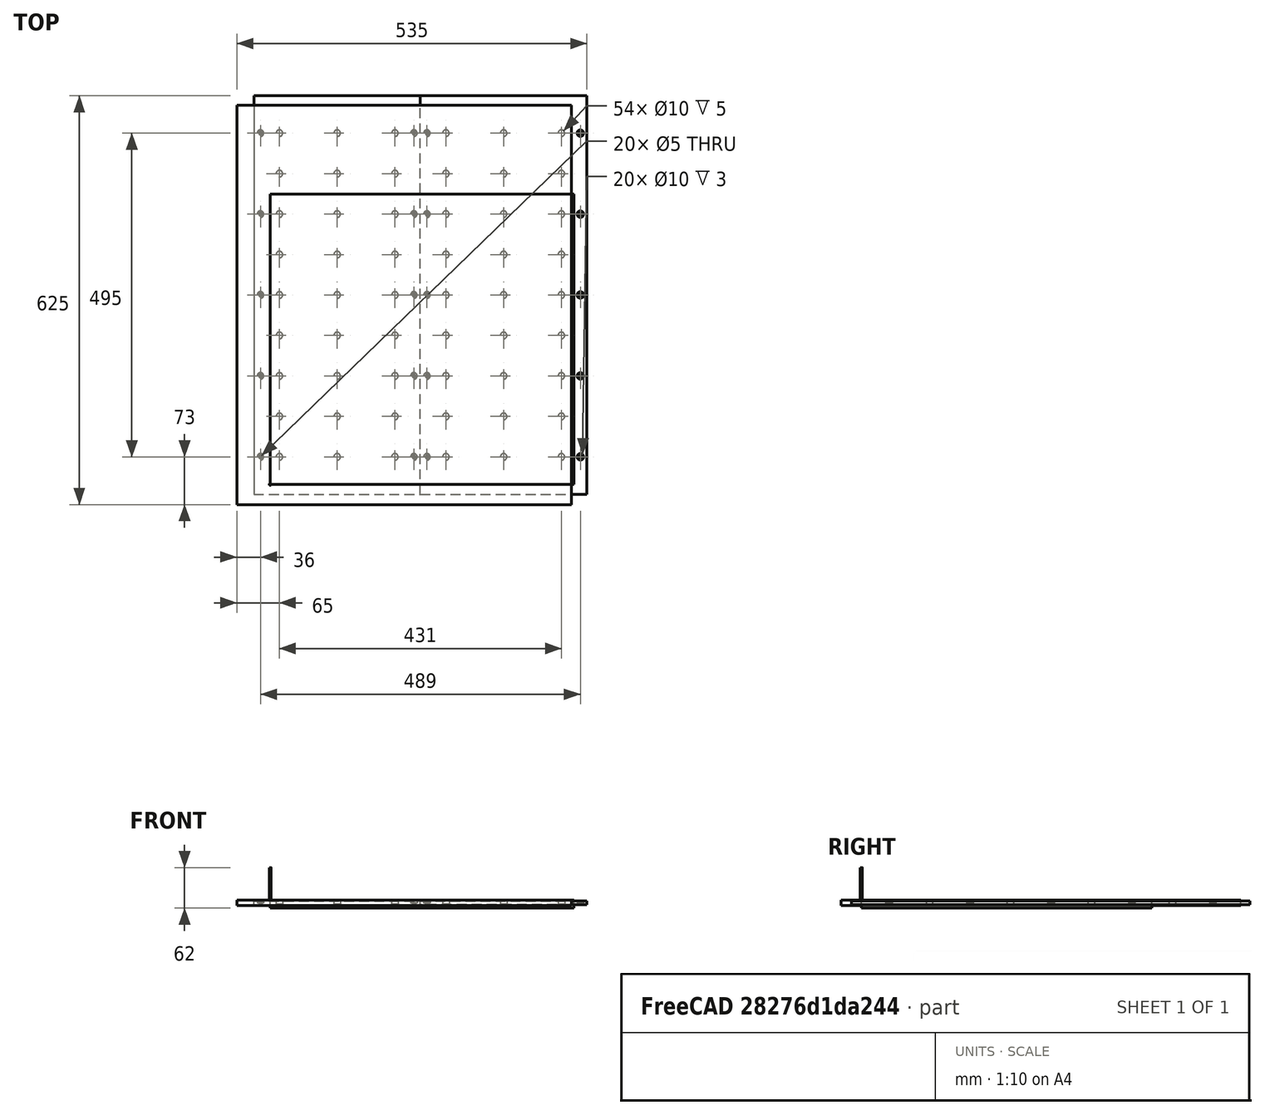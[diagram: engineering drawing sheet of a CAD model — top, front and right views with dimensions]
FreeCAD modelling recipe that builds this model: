
FCSTD DOCUMENT  (FreeCAD 1.0R39109 (Git))
Label: ttc450-wasteboard
License: All rights reserved
LicenseURL: http://en.wikipedia.org/wiki/All_rights_reserved
objects: Part::FeaturePython×5, PartDesign::LinearPattern×4, Path::FeaturePython×4, Sketcher::SketchObject×3, App::DocumentObjectGroup×3, PartDesign::Hole×2, PartDesign::MultiTransform×2, PartDesign::Body×2, PartDesign::Pad×1, PartDesign::FeatureBase×1, App::FeaturePython×1, Mesh::FeaturePython×1
note: 36 computed .brp shape members not serialized (recipe doc carries the construction recipe); baked Part::Feature solids carry a one-line shape summary decoded from their .brp

FEATURE [Sketcher::SketchObject] Sketch
  ArcFitTolerance = 1e-06
  AttachmentSupport = -> [XY_Plane]
  FullyConstrained = true
  MakeInternals = false
  MapMode = 5
  sketch-geometry (4):
    g0: LineSegment StartX=0 StartY=0 StartZ=0 EndX=254.5 EndY=0 EndZ=0
    g1: LineSegment StartX=254.5 StartY=0 StartZ=0 EndX=254.5 EndY=609 EndZ=0
    g2: LineSegment StartX=254.5 StartY=609 StartZ=0 EndX=0 EndY=609 EndZ=0
    g3: LineSegment StartX=0 StartY=609 StartZ=0 EndX=0 EndY=0 EndZ=0
  constraints (11):
    c: Coincident(g0,g1)
    c: Coincident(g1,g2)
    c: Coincident(g2,g3)
    c: Coincident(g3,g0)
    c: Horizontal(g0)
    c: Horizontal(g2)
    c: Vertical(g1)
    c: Vertical(g3)
    c: Distance(g1,g3) = 254.5
    c: Distance(g0,g2) = 609
    c: Coincident(g0,g-1)
FEATURE [PartDesign::Pad] Pad
  Direction = (0,0,1)
  Length = 6
  Length2 = 10
  Profile = -> Sketch
  ReferenceAxis = -> Sketch [N_Axis]
  Suppressed = false
  Type = 0
FEATURE [Sketcher::SketchObject] Sketch001
  ArcFitTolerance = 1e-06
  AttachmentSupport = -> [Pad]
  FullyConstrained = true
  MakeInternals = false
  MapMode = 5
  Placement = pos=(0,0,6) rot=(0,0,1;0rad)
  sketch-geometry (1):
    g0: Circle CenterX=10 CenterY=57 CenterZ=0 NormalX=0 NormalY=0 NormalZ=1 AngleXU=0 Radius=5
  constraints (3):
    c: DistanceX(g-1,g0) = 10
    c: DistanceY(g-1,g0) = 57
    c: Diameter(g0) = 10
FEATURE [PartDesign::Hole] Hole  label="Bottom Left Fixation Hole"
  BaseFeature = -> Pad
  CustomThreadClearance = 0
  Depth = 25
  DepthType = 0
  Diameter = 5
  DrillForDepth = false
  DrillPoint = 1
  DrillPointAngle = 118
  HoleCutCountersinkAngle = 90
  HoleCutCustomValues = false
  HoleCutDepth = 3
  HoleCutDiameter = 10
  HoleCutType = 1
  ModelThread = false
  Profile = -> Sketch001 [Edge1]
  Suppressed = false
  Tapered = false
  TaperedAngle = 90
  ThreadClass = 0
  ThreadDepth = 25
  ThreadDepthType = 0
  ThreadDirection = 0
  ThreadFit = 0
  ThreadSize = 0
  ThreadType = 0
  Threaded = false
  UseCustomThreadClearance = false
FEATURE [PartDesign::LinearPattern] LinearPattern
  Direction = -> Sketch001 [H_Axis]
  Length = 234.5
  Mode = 0
  Occurrences = 2
  Offset = 234.5
  Suppressed = false
  TransformMode = 0
FEATURE [PartDesign::LinearPattern] LinearPattern001
  Direction = -> Y_Axis
  Length = 990
  Mode = 1
  Occurrences = 9
  Offset = 123.75
  Suppressed = false
  TransformMode = 0
FEATURE [PartDesign::MultiTransform] MultiTransform  label="Filxation Holes MultiTransform"
  BaseFeature = -> Hole
  Originals = -> [Hole]
  Suppressed = false
  TransformMode = 0
  Transformations = -> [LinearPattern,LinearPattern001]
FEATURE [Sketcher::SketchObject] Sketch002
  ArcFitTolerance = 1e-06
  AttachmentSupport = -> [Pad]
  FullyConstrained = true
  MakeInternals = false
  MapMode = 5
  Placement = pos=(0,0,6) rot=(0,0,1;0rad)
  sketch-geometry (1):
    g0: Circle CenterX=39 CenterY=57 CenterZ=0 NormalX=0 NormalY=0 NormalZ=1 AngleXU=0 Radius=4.5
  constraints (3):
    c: Diameter(g0) = 9
    c: DistanceX(g-1,g0) = 39
    c: DistanceY(g-1,g0) = 57
FEATURE [PartDesign::Hole] Hole001  label="Bottom Left Mounting Hole"
  BaseFeature = -> MultiTransform
  CustomThreadClearance = 0
  Depth = 5
  DepthType = 0
  Diameter = 10
  DrillForDepth = false
  DrillPoint = 0
  DrillPointAngle = 118
  HoleCutCountersinkAngle = 90
  HoleCutCustomValues = false
  HoleCutDepth = 0
  HoleCutDiameter = 0
  HoleCutType = 0
  ModelThread = false
  Profile = -> Sketch002
  Suppressed = false
  Tapered = false
  TaperedAngle = 90
  ThreadClass = 0
  ThreadDepth = 5
  ThreadDepthType = 0
  ThreadDirection = 0
  ThreadFit = 0
  ThreadSize = 0
  ThreadType = 0
  Threaded = false
  UseCustomThreadClearance = false
FEATURE [PartDesign::LinearPattern] LinearPattern002
  Direction = -> Sketch002 [H_Axis]
  Length = 176.5
  Mode = 1
  Occurrences = 3
  Offset = 88.25
  Suppressed = false
  TransformMode = 0
FEATURE [PartDesign::LinearPattern] LinearPattern003
  Direction = -> Sketch002 [V_Axis]
  Length = 495
  Mode = 1
  Occurrences = 9
  Offset = 61.875
  Suppressed = false
  TransformMode = 0
FEATURE [PartDesign::MultiTransform] MultiTransform001  label="Mounting Holes MultiTransform"
  BaseFeature = -> Hole001
  Originals = -> [Hole001]
  Suppressed = false
  TransformMode = 0
  Transformations = -> [LinearPattern002,LinearPattern003]
FEATURE [PartDesign::Body] Body  label="Left Panel"
  AllowCompound = false
  Group = -> [Sketch,Pad,Sketch001,Hole,MultiTransform,LinearPattern,LinearPattern001,Sketch002,Hole001,MultiTransform001,LinearPattern002,LinearPattern003]
  Origin = -> Origin
  Tip = -> MultiTransform001
FEATURE [PartDesign::FeatureBase] Clone
  BaseFeature = -> Body
  Suppressed = false
FEATURE [PartDesign::Body] Body001  label="Right Panel"
  AllowCompound = false
  Group = -> [Clone]
  Origin = -> Origin001
  Placement = pos=(254.5,0,0) rot=(0,0,1;0rad)
  Tip = -> Clone
FEATURE [App::FeaturePython] SetupSheet  # Path/CAM operation (typed FeaturePython)
  ClearanceHeightExpression = OpStockZMax+SetupSheet.ClearanceHeightOffset
  ClearanceHeightOffset = 5
  CoolantMode = 0
  CoolantModes = None | Flood | Mist
  FinalDepthExpression = OpFinalDepth
  HorizRapid = 0
  SafeHeightExpression = OpStockZMax+SetupSheet.SafeHeightOffset
  SafeHeightOffset = 3
  StartDepthExpression = OpStartDepth
  StepDownExpression = OpToolDiameter/3
  VertRapid = 0
FEATURE [Part::FeaturePython] Clone001  label="Model-Left Panel"  # Draft clone (typed FeaturePython)
  AttacherType = Attacher::AttachEngine3D
  Fuse = false
  Objects = -> [Body]
  PathResource = Model
  Placement = pos=(-25,-15,-7) rot=(0,0,1;0rad)
  Scale = (1,1,1)
FEATURE [Part::FeaturePython] Clone002  label="Model-Right Panel"  # Draft clone (typed FeaturePython)
  AttacherType = Attacher::AttachEngine3D
  Fuse = false
  Objects = -> [Body001]
  PathResource = Model
  Placement = pos=(229.5,-15,-7) rot=(0,0,1;0rad)
  Scale = (1,1,1)
FEATURE [App::DocumentObjectGroup] Model
  Group = -> [Clone001,Clone002]
FEATURE [Part::FeaturePython] ToolBit001  label="3mm Endmil"  # Path/CAM toolbit (typed FeaturePython)
  BitPropertyNames = Chipload | CuttingEdgeHeight | Diameter | Flutes | Length | Material | ShankDiameter | SpindleDirection
  BitShape = <userpath>/.local/share/FreeCAD/Mod/CAM/Tools/Shape/endmill.fcstd
  Chipload = 0
  CuttingEdgeHeight = 30
  Diameter = 3
  File = <userpath>/.local/share/FreeCAD/Mod/CAM/Tools/Bit/3mm_Endmill.fctb
  Flutes = 0
  Length = 50
  Material = 0
  ShankDiameter = 3
  ShapeName = endmill
  SpindleDirection = 0
FEATURE [Path::FeaturePython] _mm_Endmil  label="3mm Endmil001"  # Path/CAM operation (typed FeaturePython)
  HorizFeed = 10
  HorizRapid = 0
  SpindleDir = 0
  SpindleSpeed = 18000
  Tool = -> ToolBit001
  ToolNumber = 2
  VertFeed = 10
  VertRapid = 0
  expr: HorizRapid = SetupSheet.HorizRapid
  expr: VertRapid = SetupSheet.VertRapid
FEATURE [App::DocumentObjectGroup] Tools
  Group = -> [_mm_Endmil]
FEATURE [Path::FeaturePython] Helix  # Path/CAM operation (typed FeaturePython)
  Active = true
  Base = -> [Clone001,Clone002]
  ClearanceHeight = 5
  CoolantMode = 0
  CutMode = 0
  CycleTime = 00:19:49
  Direction = 0
  FinalDepth = -5
  OffsetExtra = 0
  OpFinalDepth = -4
  OpStartDepth = 0
  OpStockZMax = 0
  OpStockZMin = -8
  OpToolDiameter = 3
  SafeHeight = 3
  StartDepth = 0
  StartRadius = 0
  StartSide = 0
  StepDown = 3
  StepOver = 50
  ToolController = -> _mm_Endmil
  expr: ClearanceHeight = OpStockZMax + SetupSheet.ClearanceHeightOffset
  expr: SafeHeight = OpStockZMax + SetupSheet.SafeHeightOffset
  expr: StepDown = OpToolDiameter
FEATURE [Part::FeaturePython] Stock001  # WARN: FeaturePython — macro-defined, semantics opaque (R4)
  Base = -> Model
  ExtXneg = -25
  ExtXpos = -20
  ExtYneg = -15
  ExtYpos = -150
  ExtZneg = 5
  ExtZpos = 1
  Placement = pos=(-25,-15,-7) rot=(0,0,1;0rad)
  StockType = FromBase
FEATURE [Path::FeaturePython] DressupPathBoundary  # Path/CAM operation (typed FeaturePython)
  Base = -> Helix
  Inside = true
  Stock = -> Stock001
FEATURE [App::DocumentObjectGroup] Operations
  Group = -> [DressupPathBoundary]
FEATURE [Part::FeaturePython] Stock  # WARN: FeaturePython — macro-defined, semantics opaque (R4)
  Base = -> Model
  ExtXneg = 1
  ExtXpos = 1
  ExtYneg = 1
  ExtYpos = 1
  ExtZneg = 1
  ExtZpos = 1
  Placement = pos=(-50,-30,-7) rot=(0,0,1;0rad)
  StockType = FromBase
FEATURE [Path::FeaturePython] Job  # Path/CAM operation (typed FeaturePython)
  CycleTime = 00:19:49
  Fixtures = G54
  GeometryTolerance = 0.01
  JobType = 0
  Model = -> Model
  Operations = -> Operations
  OrderOutputBy = 1
  PostProcessor = 11
  PostProcessorOutputFile = <userpath>/repos/perso/ttc450/wasteboard/ttc450-wasteboard.nc
  SetupSheet = -> SetupSheet
  SplitOutput = false
  Stock = -> Stock
  Tools = -> Tools
FEATURE [Mesh::FeaturePython] CutMaterial  # WARN: FeaturePython — macro-defined, semantics opaque (R4)
